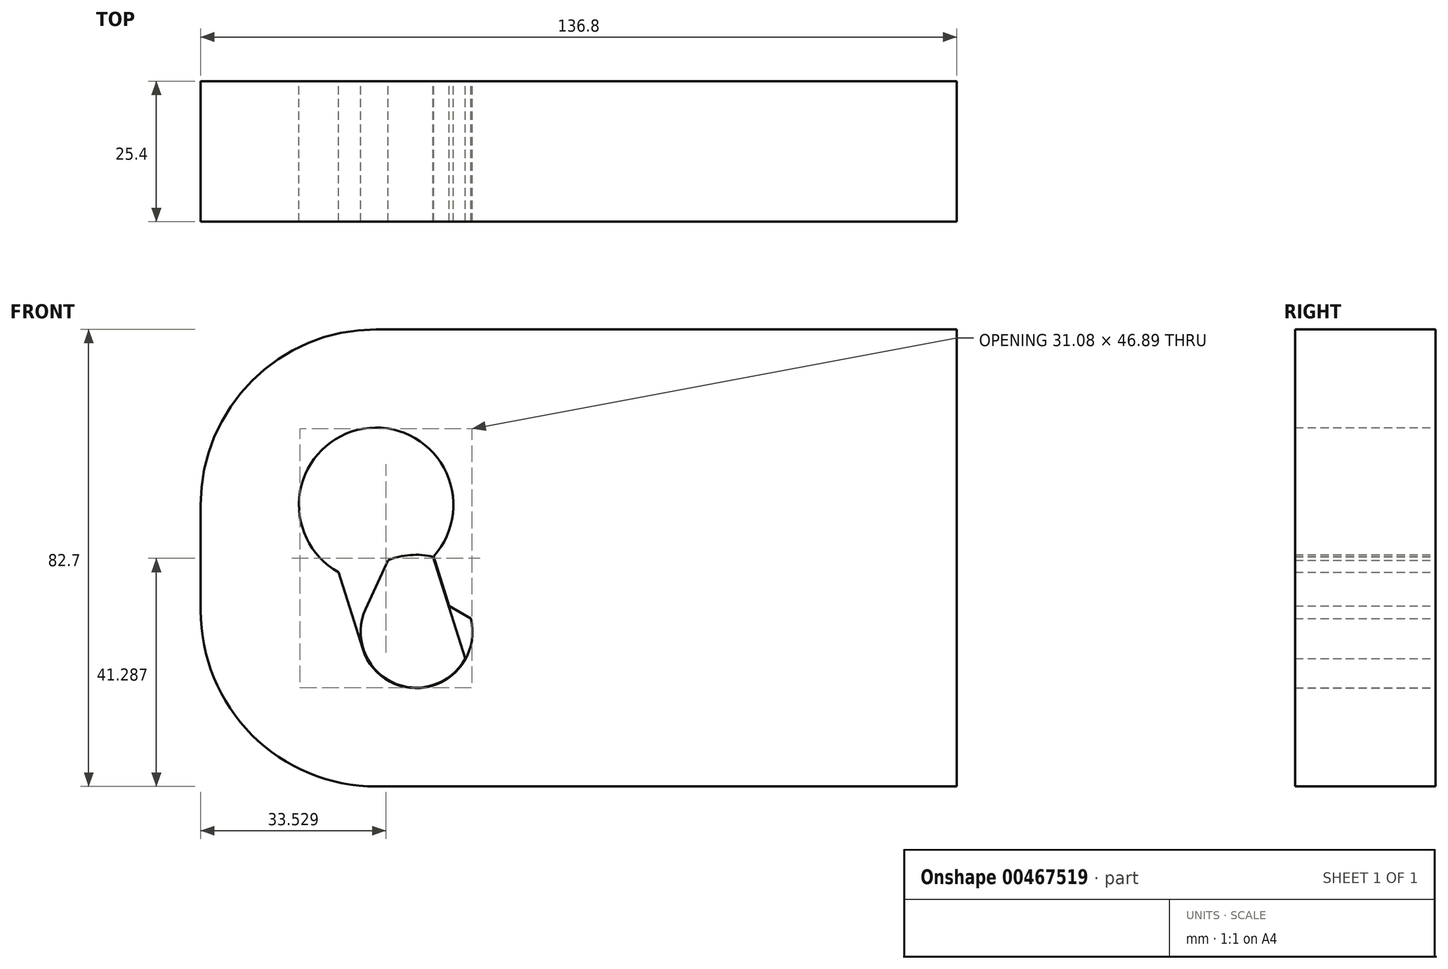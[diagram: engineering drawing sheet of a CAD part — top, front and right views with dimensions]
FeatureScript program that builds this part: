
annotation { "Feature Type Name" : "Feature", "Feature Type Description" : "" }
export const myFeature = defineFeature(function(context is Context, id is Id, definition is map)
    precondition{}
    {
        {
            var Q0;
            Q0=qCreatedBy(makeId("Front.planeOp"),FACE);
            var sketch = newSketch(context, id + "F0", { "sketchPlane" : qUnion([Q0])});
            skCircle(sketch, "E0", {"center": v(0, 0) * mm, "radius": 10.16 * mm});
            skLineSegment(sketch, "E1", {"start": v(0, 0) * mm, "end": v(0, 63.5) * mm, "construction": true});
            skLineSegment(sketch, "E2", {"start": v(0, 0) * mm, "end": v(-19.1, 60.56) * mm, "construction": true});
            skLineSegment(sketch, "E3", {"start": v(0, 0) * mm, "end": v(-7.26, 23.01) * mm, "construction": true});
            skCircle(sketch, "E4", {"center": v(-7.26, 23.01) * mm, "radius": 13.97 * mm});
            skLineSegment(sketch, "E5", {"start": v(0, 0) * mm, "end": v(-9.69, -3.06) * mm, "construction": true});
            skLineSegment(sketch, "E6", {"start": v(-9.69, -3.06) * mm, "end": v(-14.06, 10.81) * mm});
            skLineSegment(sketch, "E7", {"start": v(0, 0) * mm, "end": v(9.69, 3.06) * mm, "construction": true});
            skLineSegment(sketch, "E8", {"start": v(9.69, 3.06) * mm, "end": v(-4.9, 49.33) * mm, "construction": true});
            skLineSegment(sketch, "E9", {"start": v(9.69, 3.06) * mm, "end": v(6.78, 2.14) * mm, "construction": true});
            skLineSegment(sketch, "E10", {"start": v(6.78, 2.14) * mm, "end": v(3.14, 13.68) * mm, "construction": true});
            skLineSegment(sketch, "E11", {"start": v(3.14, 13.68) * mm, "end": v(4.6, 9.06) * mm});
            skLineSegment(sketch, "E12", {"start": v(0, -10.16) * mm, "end": v(0, -27.94) * mm, "construction": true});
            skLineSegment(sketch, "E13", {"start": v(-7.26, 23.01) * mm, "end": v(-21.23, 23.01) * mm, "construction": true});
            skLineSegment(sketch, "E14", {"start": v(-21.23, 23.01) * mm, "end": v(-39, 23.01) * mm, "construction": true});
            skLineSegment(sketch, "E15", {"start": v(-7.26, 36.98) * mm, "end": v(-7.26, 54.76) * mm, "construction": true});
            skArc(sketch, "E16", {"start": v(-7.26, 54.76) * mm, "mid": v(-29.7, 45.46) * mm, "end": v(-39, 23.01) * mm});
            skLineSegment(sketch, "E17", {"start": v(0, -27.94) * mm, "end": v(-7.26, -27.94) * mm, "construction": true});
            skLineSegment(sketch, "E18", {"start": v(-7.26, -27.94) * mm, "end": v(-7.26, 3.8) * mm, "construction": true});
            skArc(sketch, "E19", {"start": v(-39, 3.88) * mm, "mid": v(-29.73, -18.62) * mm, "end": v(-7.26, -27.94) * mm});
            skPoint(sketch, "E19.startSnap0", {"position": v(-11.88, 3.88) * mm});
            skLineSegment(sketch, "E20", {"start": v(-39, 23.01) * mm, "end": v(-39, 3.88) * mm});
            skLineSegment(sketch, "E21", {"start": v(-7.26, 54.76) * mm, "end": v(0, 54.76) * mm});
            skLineSegment(sketch, "E22", {"start": v(-7.26, -27.94) * mm, "end": v(0, -27.94) * mm});
            skLineSegment(sketch, "E23", {"start": v(0, 54.76) * mm, "end": v(97.8, 54.76) * mm});
            skLineSegment(sketch, "E24", {"start": v(97.8, 54.76) * mm, "end": v(97.8, -27.94) * mm});
            skLineSegment(sketch, "E25", {"start": v(97.8, -27.94) * mm, "end": v(0, -27.94) * mm});
            skLineSegment(sketch, "E26", {"start": v(0, 0) * mm, "end": v(5.16, 8.75) * mm, "construction": true});
            skLineSegment(sketch, "E27", {"start": v(5.16, 8.75) * mm, "end": v(3.6, 6.13) * mm, "construction": true});
            skLineSegment(sketch, "E28", {"start": v(3.6, 6.13) * mm, "end": v(9.86, 2.45) * mm, "construction": true});
            skLineSegment(sketch, "E29", {"start": v(9.86, 2.45) * mm, "end": v(5.96, 4.74) * mm});
            skLineSegment(sketch, "E30", {"start": v(5.96, 4.74) * mm, "end": v(4.6, 9.06) * mm});
            skSolve(sketch);
        }
        {
            var Q0;
            Q0=qCreatedBy(makeId("Front.planeOp"),FACE);
            var sketch = newSketch(context, id + "F1", { "sketchPlane" : qUnion([Q0])});
            skCircle(sketch, "E31", {"center": v(0, 0) * mm, "radius": 10.06 * mm});
            skLineSegment(sketch, "E32", {"start": v(0, 0) * mm, "end": v(9.6, 3.02) * mm, "construction": true});
            skLineSegment(sketch, "E33", {"start": v(9.6, 3.02) * mm, "end": v(6.69, 2.1) * mm, "construction": true});
            skLineSegment(sketch, "E34", {"start": v(6.69, 2.1) * mm, "end": v(4.52, 8.99) * mm, "construction": true});
            skLineSegment(sketch, "E35", {"start": v(4.52, 8.99) * mm, "end": v(8.85, -4.77) * mm});
            skCircle(sketch, "E36", {"center": v(0, 0) * mm, "radius": 13.97 * mm, "construction": true});
            skLineSegment(sketch, "E37", {"start": v(4.52, 8.99) * mm, "end": v(3.05, 13.63) * mm});
            skLineSegment(sketch, "E38", {"start": v(0, 0) * mm, "end": v(-9.15, 4.17) * mm, "construction": true});
            skLineSegment(sketch, "E39", {"start": v(-9.15, 4.17) * mm, "end": v(-5.13, 13) * mm, "construction": true});
            skLineSegment(sketch, "E40", {"start": v(-9.15, 4.17) * mm, "end": v(-5.13, 13) * mm});
            skArc(sketch, "E41", {"start": v(3.05, 13.63) * mm, "mid": v(-1.09, 13.93) * mm, "end": v(-5.13, 13) * mm});
            skSolve(sketch);
        }
        {
            var Q0;
            {var subQ3=sQuery(id+"F0.wireOp",EDGE,"E6");Q0=makeQuery(id+"F0.imprint","IMPRINT",FACE,{"disambiguationData":[TD([[makeQuery(id+"F0.imprint","IMPRINT",EDGE,{"derivedFrom":subQ3}),1.0]])]});}
            var Q1;
            {var subQ2=sQuery(id+"F0.wireOp",EDGE,"E29");Q1=makeQuery(id+"F0.imprint","IMPRINT",FACE,{"disambiguationData":[TD([[makeQuery(id+"F0.imprint","IMPRINT",EDGE,{"derivedFrom":subQ2}),-1.0]])]});}
            extrude(context, id + "F2", {"entities" : qUnion([Q0, Q1]), "depth" : 25.4 * mm});
        }
        {
            var Q0;
            {var subQ0=sQuery(id+"F1.wireOp",EDGE,"E35");Q0=makeQuery(id+"F1.imprint","IMPRINT",FACE,{"disambiguationData":[TD([[makeQuery(id+"F1.imprint","IMPRINT",EDGE,{"derivedFrom":subQ0}),-1.0]])]});}
            var Q1;
            {var subQ0=sQuery(id+"F1.wireOp",EDGE,"E37");Q1=makeQuery(id+"F1.imprint","IMPRINT",FACE,{"disambiguationData":[TD([[makeQuery(id+"F1.imprint","IMPRINT",EDGE,{"derivedFrom":subQ0}),1.0]])]});}
            extrude(context, id + "F3", {"entities" : qUnion([Q0, Q1]), "depth" : 25.4 * mm});
        }
    });
